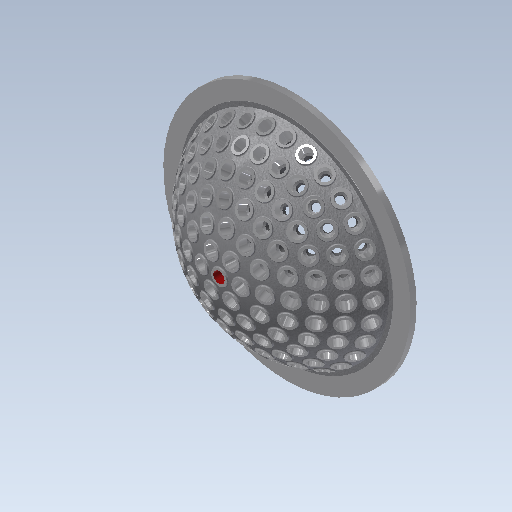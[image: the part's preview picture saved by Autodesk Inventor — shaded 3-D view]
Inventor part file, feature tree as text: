
AUTODESK INVENTOR PART (.ipt)
format: ipt  version: 2020.1 (Build 241239000, 239)  size: 1,890,304 bytes
history: native  units: mm
features: plane x15, hole x14, sketch x9, extrude x7, fillet x7, pattern_circular x6, revolve x2, shell x1, split x1, other x1
ambient origin geometry x8: Origin, YZ Plane, XZ Plane, XY Plane, X Axis, Y Axis, Z Axis, Center Point
bodies: Solid1 (feature_tree)
feature tree (63):
  revolve  "Revolution1"  Angle=180.0deg
  shell  "Shell1"  Thickness=16.0mm
  plane  "Work Plane1"
  extrude  "Extrusion1"  Depth=10.0mm
  fillet  "Fillet1"  Radius=10.0mm
  hole  "Hole1"  [1 undecoded]
  hole  "Hole2"  [1 undecoded]
  plane  "Work Plane4"
  extrude  "Extrusion2"  Depth=10.0mm
  fillet  "Fillet2"  Radius=10.0mm
  hole  "Hole3"  [1 undecoded]
  hole  "Hole4"  [1 undecoded]
  pattern_circular  "Circular Pattern1"  [2 undecoded]
  plane  "Work Plane7"
  extrude  "Extrusion3"  Depth=0.5mm
  fillet  "Fillet3"  Radius=10.0mm
  hole  "Hole5"  [1 undecoded]
  hole  "Hole6"  [1 undecoded]
  pattern_circular  "Circular Pattern2"  Count=12 Angle=360.0deg
  plane  "Work Plane9"
  extrude  "Extrusion4"  Depth=101.0mm TaperAngle=30.0deg
  fillet  "Fillet4"  Radius=14.0mm
  hole  "Hole7"  [1 undecoded]
  hole  "Hole8"  [1 undecoded]
  pattern_circular  "Circular Pattern3"  [2 undecoded]
  plane  "Work Plane11"
  extrude  "Extrusion5"  Depth=10.0mm
  fillet  "Fillet5"  Radius=180.0mm
  hole  "Hole9"  [1 undecoded]
  hole  "Hole10"  [1 undecoded]
  pattern_circular  "Circular Pattern4"  [2 undecoded]
  plane  "Work Plane13"
  extrude  "Extrusion6"  Depth=0.8mm
  fillet  "Fillet6"  Radius=10.0mm
  hole  "Hole11"  [1 undecoded]
  hole  "Hole12"  [1 undecoded]
  pattern_circular  "Circular Pattern5"  [2 undecoded]
  plane  "Work Plane15"
  extrude  "Extrusion7"  Depth=0.5mm
  fillet  "Fillet7"  Radius=10.0mm
  hole  "Hole13"  [1 undecoded]
  hole  "Hole14"  [1 undecoded]
  pattern_circular  "Circular Pattern6"  [2 undecoded]
  plane  "Work Plane16"
  split  "Split1"
  revolve  "Revolution2"  Angle=360.0deg
  sketch  "Sketch1"  dims[d0=100.0mm d1=180.0deg d2=16.0mm]
  sketch  "Sketch2"  dims[d3=101.0mm d4=14.0mm d5=10.0mm d6=0.0mm]
  plane  "Work Plane2"
  other  "Work Axis1"
  plane  "Work Plane3"
  sketch  "Sketch3"  dims[d7=0.8mm]
  plane  "Work Plane6"
  sketch  "Sketch4"  dims[d81=10.0mm d82=10.0mm d10=10.0mm d11=6.0mm d12=4.0mm d13=2.0mm d14=90.0deg d15=10.0mm d16=20.594885mm d17=10.0mm d18=10.0mm]
  plane  "Work Plane8"
  sketch  "Sketch5"  dims[d19=6.647mm d20=6.0mm d21=4.0mm d22=2.0mm d23=90.0deg d24=15.0mm d25=20.594885mm d26=-13.962634mm]
  plane  "Work Plane10"
  sketch  "Sketch6"  dims[d27=101.0mm d28=14.0mm d29=10.0mm d30=0.0mm]
  plane  "Work Plane12"
  sketch  "Sketch7"  dims[d31=0.8mm d32=10.0mm d33=10.0mm]
  plane  "Work Plane14"
  sketch  "Sketch8"  dims[d34=6.647mm d35=6.0mm d36=4.0mm d37=2.0mm d38=90.0deg d39=15.0mm d40=20.594885mm]
  sketch  "Sketch9"  dims[d83=10.0mm d84=10.0mm d43=10.0mm d44=6.0mm d45=4.0mm d46=2.0mm d47=90.0deg d48=10.0mm d49=20.594885mm d50=60.0mm d51=360.0deg d54=3.490659mm d55=101.0mm d56=14.0mm d57=10.0mm d58=0.0mm d59=0.8mm d85=10.0mm d86=10.0mm d62=10.0mm d63=6.0mm d64=4.0mm d65=2.0mm d66=90.0deg d67=10.0mm d68=20.594885mm d69=10.0mm d70=10.0mm d71=6.647mm d72=6.0mm d73=4.0mm d74=2.0mm d75=90.0deg d76=15.0mm d77=20.594885mm d78=120.0mm d79=360.0deg d87=30.0deg d88=101.0mm d89=14.0mm d90=10.0mm d91=0.0mm d92=0.8mm d93=10.0mm d94=10.0mm d95=10.0mm d96=6.0mm d97=4.0mm d98=2.0mm d99=90.0deg d100=10.0mm d101=20.594885mm d102=10.0mm d103=10.0mm d104=6.647mm d105=6.0mm d106=4.0mm d107=2.0mm d108=90.0deg d109=10.0mm d110=20.594885mm d111=180.0mm d112=360.0deg d114=6.981317mm d115=101.0mm d116=14.0mm d117=10.0mm d118=0.0mm d119=0.8mm d120=10.0mm d121=10.0mm d122=6.647mm d123=6.0mm d124=4.0mm d125=2.0mm d126=90.0deg d127=10.0mm d128=20.594885mm d129=10.0mm d130=10.0mm d131=10.0mm d132=6.0mm d133=4.0mm d134=2.0mm d135=90.0deg d136=10.0mm d137=20.594885mm d138=240.0mm d139=360.0deg d141=8.726646mm d142=101.0mm d143=14.0mm d144=10.0mm d145=0.0mm d146=0.8mm d147=10.0mm d148=10.0mm d149=10.0mm d150=6.0mm d151=4.0mm d152=2.0mm d153=90.0deg d154=10.0mm d155=20.594885mm d156=10.0mm d157=10.0mm d158=6.647mm d159=6.0mm d160=4.0mm d161=2.0mm d162=90.0deg d163=10.0mm d164=20.594885mm d165=280.0mm d166=360.0deg d168=60.0deg d169=101.0mm d170=14.0mm d171=10.0mm d172=0.0mm d173=0.8mm d174=10.0mm d175=10.0mm d176=6.647mm d177=6.0mm d178=4.0mm d179=2.0mm d180=90.0deg d181=10.0mm d182=20.594885mm d183=10.0mm d184=10.0mm d185=10.0mm d186=6.0mm d187=4.0mm d188=2.0mm d189=90.0deg d190=10.0mm d191=20.594885mm d192=300.0mm d193=360.0deg d195=-35.0mm d199=6.0mm d200=220.0mm d202=190.0mm d203=90.0deg d212=0.5mm]
note: 24 required parameter values undecoded (feature->parameter linkage not recoverable at this tier; creation-order binding heuristic only, values carry confidence <= 0.55)
